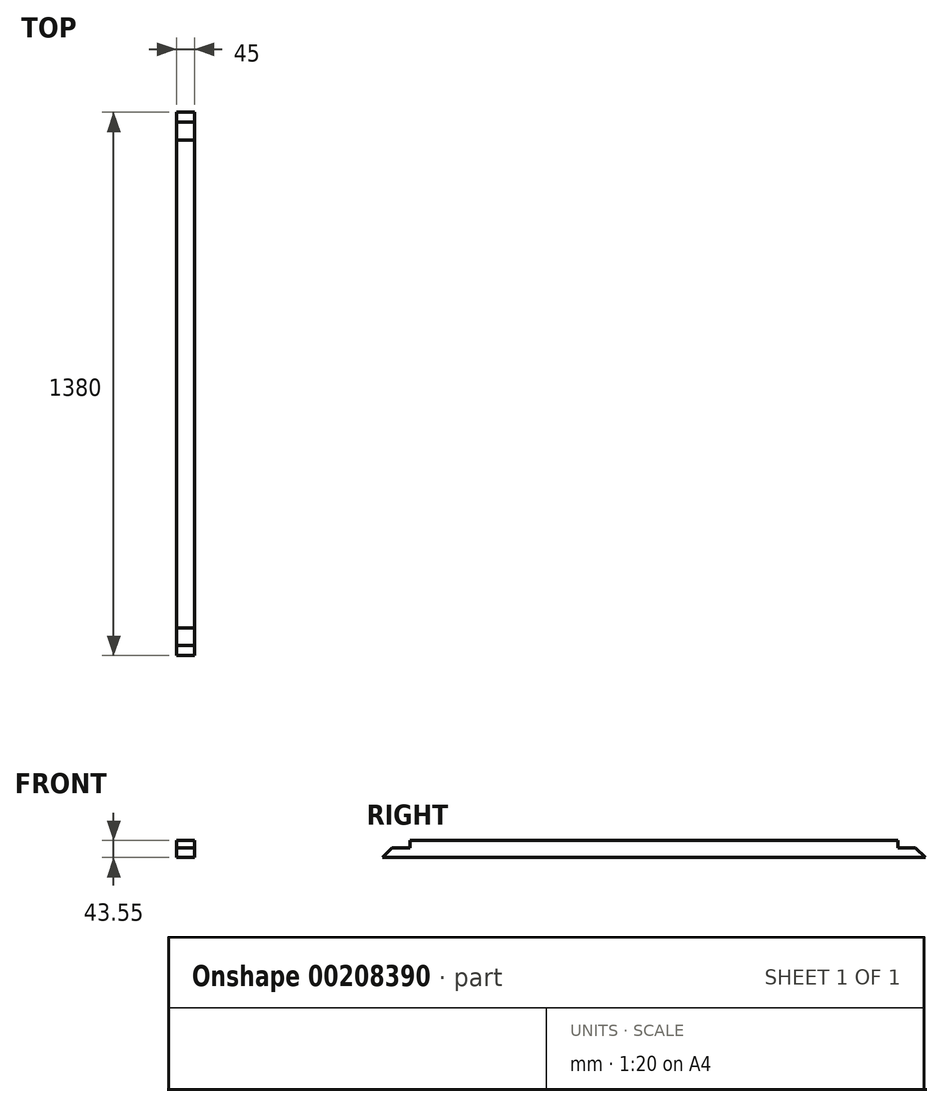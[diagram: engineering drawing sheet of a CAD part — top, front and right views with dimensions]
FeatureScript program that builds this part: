
annotation { "Feature Type Name" : "Feature", "Feature Type Description" : "" }
export const myFeature = defineFeature(function(context is Context, id is Id, definition is map)
    precondition{}
    {
        {
            var Q0;
            Q0=qCreatedBy(makeId("Front.planeOp"),FACE);
            var sketch = newSketch(context, id + "F0", { "sketchPlane" : qUnion([Q0])});
            skLineSegment(sketch, "E0.bottom", {"start": v(-22.5, 12.5) * mm, "end": v(22.5, 12.5) * mm});
            skLineSegment(sketch, "E0.top", {"start": v(-22.5, -12.5) * mm, "end": v(22.5, -12.5) * mm});
            skLineSegment(sketch, "E0.left", {"start": v(-22.5, 12.5) * mm, "end": v(-22.5, -12.5) * mm});
            skLineSegment(sketch, "E0.right", {"start": v(22.5, 12.5) * mm, "end": v(22.5, -12.5) * mm});
            skSolve(sketch);
        }
        {
            var Q0;
            Q0=makeQuery(id+"F0.imprint","IMPRINT",FACE,{"disambiguationData":[TD([[makeQuery(id+"F0.imprint","IMPRINT",EDGE,{"derivedFrom":sQuery(id+"F0.wireOp",EDGE,"E0.bottom")}),-1.0]])]});
            extrude(context, id + "F1", {"entities" : qUnion([Q0]), "oppositeDirection" : true, "depth" : 1380 * mm});
        }
        {
            var Q0;
            Q0=makeQuery(id+"F1.opExtrude","SWEPT_FACE",FACE,{"disambiguationData":[OSD([sQuery(id+"F0.wireOp",EDGE,"E0.right")])]});
            var sketch = newSketch(context, id + "F2", { "sketchPlane" : qUnion([Q0])});
            skLineSegment(sketch, "E1", {"start": v(0, -12.5) * mm, "end": v(25, 12.5) * mm});
            skLineSegment(sketch, "E2", {"start": v(25, 12.5) * mm, "end": v(0, 12.5) * mm});
            skLineSegment(sketch, "E3", {"start": v(0, 12.5) * mm, "end": v(0, -12.5) * mm});
            skSolve(sketch);
        }
        {
            var Q0;
            Q0=makeQuery(id+"F2.imprint","IMPRINT",FACE,{"disambiguationData":[TD([[makeQuery(id+"F2.imprint","IMPRINT",EDGE,{"derivedFrom":sQuery(id+"F2.wireOp",EDGE,"E1")}),1.0]])]});
            extrude(context, id + "F3", {"entities" : qUnion([Q0]), "operationType" : NewBodyOperationType.REMOVE, "oppositeDirection" : true, "depth" : 45 * mm});
        }
        {
            var Q0;
            Q0=makeQuery(id+"F1.opExtrude","SWEPT_FACE",FACE,{"disambiguationData":[OSD([sQuery(id+"F0.wireOp",EDGE,"E0.left")])]});
            var sketch = newSketch(context, id + "F4", { "sketchPlane" : qUnion([Q0])});
            skLineSegment(sketch, "E4", {"start": v(-1380, -12.5) * mm, "end": v(-1355, 12.5) * mm});
            skLineSegment(sketch, "E5", {"start": v(-1355, 12.5) * mm, "end": v(-1380, 12.5) * mm});
            skLineSegment(sketch, "E6", {"start": v(-1380, 12.5) * mm, "end": v(-1380, -12.5) * mm});
            skSolve(sketch);
        }
        {
            var Q0;
            Q0=makeQuery(id+"F4.imprint","IMPRINT",FACE,{"disambiguationData":[TD([[makeQuery(id+"F4.imprint","IMPRINT",EDGE,{"derivedFrom":sQuery(id+"F4.wireOp",EDGE,"E4")}),1.0]])]});
            extrude(context, id + "F5", {"entities" : qUnion([Q0]), "operationType" : NewBodyOperationType.REMOVE, "oppositeDirection" : true, "depth" : 45 * mm});
        }
        {
            var Q0;
            Q0=qCreatedBy(makeId("Front.planeOp"),FACE);
            var sketch = newSketch(context, id + "F6", { "sketchPlane" : qUnion([Q0])});
            skLineSegment(sketch, "E7.bottom", {"start": v(-22.5, 31.05) * mm, "end": v(22.5, 31.05) * mm});
            skLineSegment(sketch, "E7.top", {"start": v(-22.5, 12.5) * mm, "end": v(22.5, 12.5) * mm});
            skLineSegment(sketch, "E7.left", {"start": v(-22.5, 31.05) * mm, "end": v(-22.5, 12.5) * mm});
            skLineSegment(sketch, "E7.right", {"start": v(22.5, 31.05) * mm, "end": v(22.5, 12.5) * mm});
            skSolve(sketch);
        }
        {
            var Q0;
            Q0=makeQuery(id+"F6.imprint","IMPRINT",FACE,{"disambiguationData":[TD([[makeQuery(id+"F6.imprint","IMPRINT",EDGE,{"derivedFrom":sQuery(id+"F6.wireOp",EDGE,"E7.bottom")}),-1.0]])]});
            extrude(context, id + "F7", {"entities" : qUnion([Q0]), "operationType" : NewBodyOperationType.ADD, "oppositeDirection" : true, "depth" : 1380 * mm});
        }
        {
            var Q0;
            Q0=makeQuery(id+"F7.boolean.opBoolean","MERGE",FACE,{"derivedFrom":[makeQuery(id+"F1.opExtrude","SWEPT_FACE",FACE,{"disambiguationData":[OSD([sQuery(id+"F0.wireOp",EDGE,"E0.right")])]}),makeQuery(id+"F7.opExtrude","SWEPT_FACE",FACE,{"disambiguationData":[OSD([sQuery(id+"F6.wireOp",EDGE,"E7.right")])]})]});
            var sketch = newSketch(context, id + "F8", { "sketchPlane" : qUnion([Q0])});
            skLineSegment(sketch, "E8.bottom", {"start": v(0, 31.05) * mm, "end": v(70, 31.05) * mm});
            skLineSegment(sketch, "E8.top", {"start": v(0, 12.5) * mm, "end": v(70, 12.5) * mm});
            skLineSegment(sketch, "E8.left", {"start": v(0, 31.05) * mm, "end": v(0, 12.5) * mm});
            skLineSegment(sketch, "E8.right", {"start": v(70, 31.05) * mm, "end": v(70, 12.5) * mm});
            skSolve(sketch);
        }
        {
            var Q0;
            Q0=makeQuery(id+"F8.imprint","IMPRINT",FACE,{"disambiguationData":[TD([[makeQuery(id+"F8.imprint","IMPRINT",EDGE,{"derivedFrom":sQuery(id+"F8.wireOp",EDGE,"E8.bottom")}),1.0]])]});
            extrude(context, id + "F9", {"entities" : qUnion([Q0]), "operationType" : NewBodyOperationType.REMOVE, "oppositeDirection" : true, "depth" : 45 * mm});
        }
        {
            var Q0;
            Q0=makeQuery(id+"F7.boolean.opBoolean","MERGE",FACE,{"derivedFrom":[makeQuery(id+"F1.opExtrude","SWEPT_FACE",FACE,{"disambiguationData":[OSD([sQuery(id+"F0.wireOp",EDGE,"E0.right")])]}),makeQuery(id+"F7.opExtrude","SWEPT_FACE",FACE,{"disambiguationData":[OSD([sQuery(id+"F6.wireOp",EDGE,"E7.right")])]})]});
            var sketch = newSketch(context, id + "F10", { "sketchPlane" : qUnion([Q0])});
            skLineSegment(sketch, "E9.bottom", {"start": v(1380, 12.5) * mm, "end": v(1310, 12.5) * mm});
            skLineSegment(sketch, "E9.top", {"start": v(1380, 31.05) * mm, "end": v(1310, 31.05) * mm});
            skLineSegment(sketch, "E9.left", {"start": v(1380, 12.5) * mm, "end": v(1380, 31.05) * mm});
            skLineSegment(sketch, "E9.right", {"start": v(1310, 12.5) * mm, "end": v(1310, 31.05) * mm});
            skSolve(sketch);
        }
        {
            var Q0;
            Q0=makeQuery(id+"F10.imprint","IMPRINT",FACE,{"disambiguationData":[TD([[makeQuery(id+"F10.imprint","IMPRINT",EDGE,{"derivedFrom":sQuery(id+"F10.wireOp",EDGE,"E9.top")}),1.0]])]});
            extrude(context, id + "F11", {"entities" : qUnion([Q0]), "operationType" : NewBodyOperationType.REMOVE, "oppositeDirection" : true, "depth" : 45 * mm});
        }
    });
